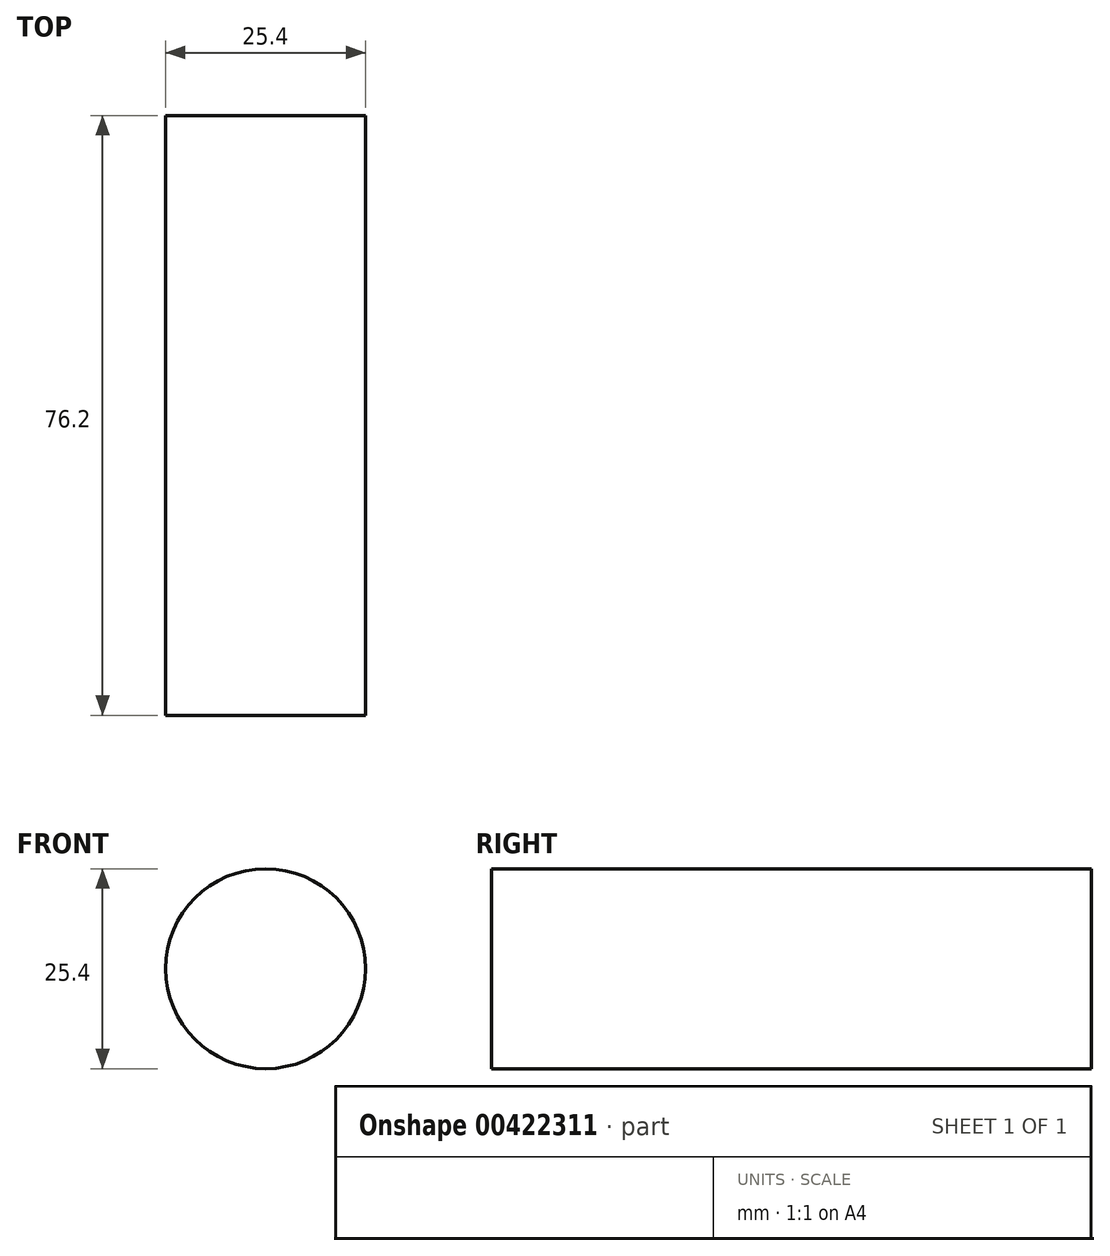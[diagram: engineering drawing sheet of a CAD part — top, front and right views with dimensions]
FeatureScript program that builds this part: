
annotation { "Feature Type Name" : "Feature", "Feature Type Description" : "" }
export const myFeature = defineFeature(function(context is Context, id is Id, definition is map)
    precondition{}
    {
        {
            var Q0;
            Q0=qCreatedBy(makeId("Front.planeOp"),FACE);
            var sketch = newSketch(context, id + "F0", { "sketchPlane" : qUnion([Q0])});
            skCircle(sketch, "E0", {"center": v(-45.07, 16.61) * mm, "radius": 12.7 * mm});
            skSolve(sketch);
        }
        {
            var Q0;
            Q0 = qSketchRegion(id + "F0", true);
            extrude(context, id + "F1", {"entities" : qUnion([Q0]), "depth" : 76.2 * mm});
        }
    });
